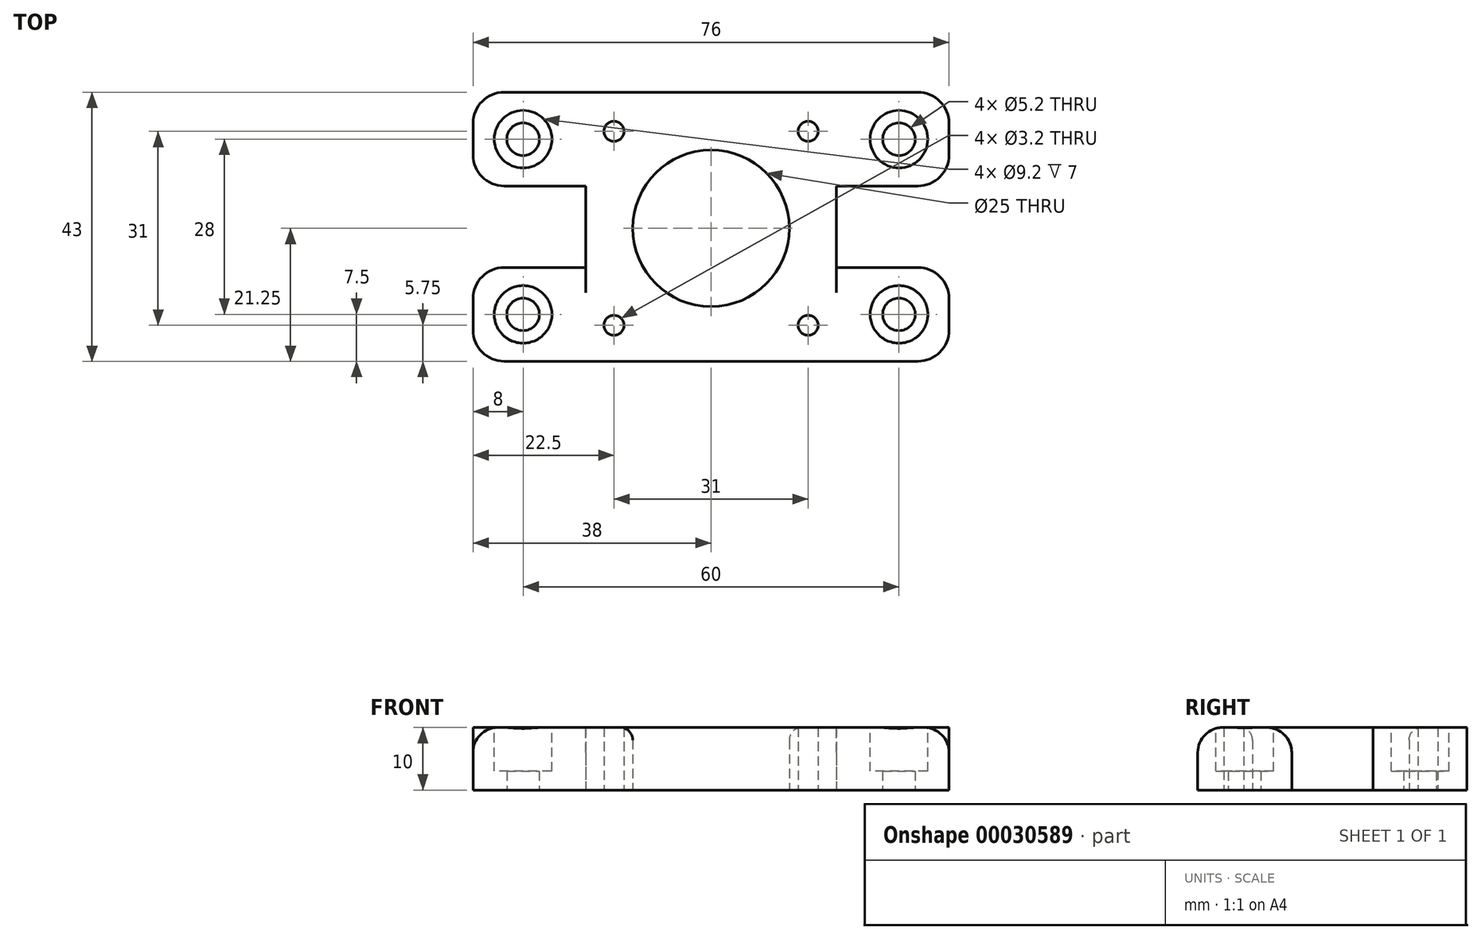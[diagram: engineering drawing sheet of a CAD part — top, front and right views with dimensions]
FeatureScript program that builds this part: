
annotation { "Feature Type Name" : "Feature", "Feature Type Description" : "" }
export const myFeature = defineFeature(function(context is Context, id is Id, definition is map)
    precondition{}
    {
        {
            assignVariable(context, id + "F0", {"name" : "defaultThickness", "anyValue" : 10 * mm});
        }
        {
            var Q0;
            Q0=qCreatedBy(makeId("Top.planeOp"),FACE);
            var sketch = newSketch(context, id + "F1", { "sketchPlane" : qUnion([Q0])});
            skLineSegment(sketch, "E0.rect.bottom", {"start": v(-20, 21.5) * mm, "end": v(20, 21.5) * mm});
            skLineSegment(sketch, "E0.rect.top", {"start": v(-20, -21.5) * mm, "end": v(20, -21.5) * mm});
            skLineSegment(sketch, "E0.rect.left", {"start": v(-20, 21.5) * mm, "end": v(-20, -21.5) * mm});
            skLineSegment(sketch, "E0.rect.right", {"start": v(20, 21.5) * mm, "end": v(20, -21.5) * mm});
            skPoint(sketch, "E0.rect.middle", {"position": v(0, 0) * mm});
            skLineSegment(sketch, "E1", {"start": v(0, 21.5) * mm, "end": v(0, 0) * mm, "construction": true});
            skLineSegment(sketch, "E2", {"start": v(0, -21.5) * mm, "end": v(0, 0) * mm, "construction": true});
            skSolve(sketch);
        }
        {
            var Q0;
            Q0 = qSketchRegion(id + "F1", true);
            extrude(context, id + "F2", {"entities" : qUnion([Q0]), "depth" : getVariable(context, 'defaultThickness')});
        }
        {
            var Q0;
            Q0=makeQuery(id+"F2.opExtrude","CAP_FACE",FACE,{"disambiguationData":[OSD([sQuery(id+"F1.wireOp",EDGE,"E0.rect.bottom"),sQuery(id+"F1.wireOp",EDGE,"E0.rect.top"),sQuery(id+"F1.wireOp",EDGE,"E0.rect.left"),sQuery(id+"F1.wireOp",EDGE,"E0.rect.right"),sQuery(id+"F1.wireOp",EDGE,"f753b575-aba3-41a6-833e-e4f93ea5e4c448.MirrorCS"),sQuery(id+"F1.wireOp",EDGE,"f753b575-aba3-41a6-833e-e4f93ea5e4c449.MirrorC"),sQuery(id+"F1.wireOp",EDGE,"f753b575-aba3-41a6-833e-e4f93ea5e4c450.MirrorCS"),sQuery(id+"F1.wireOp",EDGE,"f753b575-aba3-41a6-833e-e4f93ea5e4c451.MirrorCS"),sQuery(id+"F1.wireOp",EDGE,"bc571038-01dd-487e-b9a0-def5901bd9830.MirrorCS"),sQuery(id+"F1.wireOp",EDGE,"12bf195a-cfe4-4b15-ab7f-3f731c2d51660.MirrorCS"),sQuery(id+"F1.wireOp",EDGE,"455051b4-7426-46a8-a129-8b9c592178470.MirrorCS"),sQuery(id+"F1.wireOp",EDGE,"7dd5bb44-a427-4bdb-ba85-5ced25b216bb0.MirrorC")])],"isStart":true});
            var sketch = newSketch(context, id + "F3", { "sketchPlane" : qUnion([Q0])});
            skLineSegment(sketch, "E3", {"start": v(20, -21.5) * mm, "end": v(20, -21.5) * mm});
            skLineSegment(sketch, "E4", {"start": v(20, -21.5) * mm, "end": v(-20, -21.5) * mm, "construction": true});
            skLineSegment(sketch, "E5", {"start": v(-20, -21.5) * mm, "end": v(-20, -21.5) * mm});
            skLineSegment(sketch, "E6", {"start": v(0, 21.5) * mm, "end": v(0, 0) * mm, "construction": true});
            skLineSegment(sketch, "E7", {"start": v(0, 0) * mm, "end": v(0, -21) * mm, "construction": true});
            skLineSegment(sketch, "E8", {"start": v(0, -21) * mm, "end": v(-20, -21) * mm, "construction": true});
            skLineSegment(sketch, "E9", {"start": v(-20, -21) * mm, "end": v(-20, 21.5) * mm, "construction": true});
            skLineSegment(sketch, "E10", {"start": v(-20, 21.5) * mm, "end": v(0, 21.5) * mm, "construction": true});
            skLineSegment(sketch, "E11", {"start": v(20, 21.5) * mm, "end": v(20, -21) * mm, "construction": true});
            skLineSegment(sketch, "E12", {"start": v(20, -21) * mm, "end": v(0, -21) * mm, "construction": true});
            skLineSegment(sketch, "E13", {"start": v(-20, 0.25) * mm, "end": v(0, 0.25) * mm, "construction": true});
            skLineSegment(sketch, "E14", {"start": v(0, 0.25) * mm, "end": v(20, 0.25) * mm, "construction": true});
            skPoint(sketch, "E15", {"position": v(0, 0.25) * mm});
            skCircle(sketch, "E16", {"center": v(0, 0.25) * mm, "radius": 12.5 * mm});
            skCircle(sketch, "E17", {"center": v(-15.5, -15.25) * mm, "radius": 1.6 * mm});
            skCircle(sketch, "E18", {"center": v(15.5, -15.25) * mm, "radius": 1.6 * mm});
            skCircle(sketch, "E19", {"center": v(15.5, 15.75) * mm, "radius": 1.6 * mm});
            skCircle(sketch, "E20", {"center": v(-15.5, 15.75) * mm, "radius": 1.6 * mm});
            skSolve(sketch);
        }
        {
            var Q0;
            Q0 = qSketchRegion(id + "F3", true);
            extrude(context, id + "F4", {"entities" : qUnion([Q0]), "operationType" : NewBodyOperationType.REMOVE, "endBound" : BoundingType.THROUGH_ALL, "oppositeDirection" : true, "depth" : 25 * mm});
        }
        {
            var Q0;
            Q0=makeQuery(id+"F2.opExtrude","CAP_FACE",FACE,{"disambiguationData":[OSD([sQuery(id+"F1.wireOp",EDGE,"E0.rect.bottom"),sQuery(id+"F1.wireOp",EDGE,"E0.rect.top"),sQuery(id+"F1.wireOp",EDGE,"E0.rect.left"),sQuery(id+"F1.wireOp",EDGE,"E0.rect.right")])],"isStart":true});
            var sketch = newSketch(context, id + "F5", { "sketchPlane" : qUnion([Q0])});
            skLineSegment(sketch, "E21", {"start": v(-20, 21.5) * mm, "end": v(-38, 21.5) * mm});
            skLineSegment(sketch, "E22", {"start": v(-38, 21.5) * mm, "end": v(-38, 6.5) * mm});
            skLineSegment(sketch, "E23", {"start": v(-38, 6.5) * mm, "end": v(-20, 6.5) * mm});
            skLineSegment(sketch, "E24", {"start": v(-20, 21.5) * mm, "end": v(-20, 6.5) * mm});
            skCircle(sketch, "E25", {"center": v(-30, 14) * mm, "radius": 2.6 * mm});
            skLineSegment(sketch, "E26.MirrorCS", {"start": v(20, 21.5) * mm, "end": v(38, 21.5) * mm});
            skLineSegment(sketch, "E27.MirrorCS", {"start": v(38, 6.5) * mm, "end": v(20, 6.5) * mm});
            skCircle(sketch, "E28.MirrorC", {"center": v(30, 14) * mm, "radius": 2.6 * mm});
            skLineSegment(sketch, "E29.MirrorCS", {"start": v(20, 21.5) * mm, "end": v(20, 6.5) * mm});
            skLineSegment(sketch, "E30.MirrorCS", {"start": v(38, 21.5) * mm, "end": v(38, 6.5) * mm});
            skLineSegment(sketch, "E31", {"start": v(-20, -21.5) * mm, "end": v(-38, -21.5) * mm});
            skLineSegment(sketch, "E32", {"start": v(-38, -21.5) * mm, "end": v(-38, -6.5) * mm});
            skLineSegment(sketch, "E33", {"start": v(-38, -6.5) * mm, "end": v(-20, -6.5) * mm});
            skLineSegment(sketch, "E34", {"start": v(-20, -6.5) * mm, "end": v(-20, -21.5) * mm});
            skLineSegment(sketch, "E35.bottom", {"start": v(20, -21.5) * mm, "end": v(38, -21.5) * mm});
            skLineSegment(sketch, "E35.top", {"start": v(20, -6.5) * mm, "end": v(38, -6.5) * mm});
            skLineSegment(sketch, "E35.left", {"start": v(20, -21.5) * mm, "end": v(20, -6.5) * mm});
            skLineSegment(sketch, "E35.right", {"start": v(38, -21.5) * mm, "end": v(38, -6.5) * mm});
            skCircle(sketch, "E36", {"center": v(-30, -14) * mm, "radius": 2.6 * mm});
            skCircle(sketch, "E37", {"center": v(30, -14) * mm, "radius": 2.6 * mm});
            skSolve(sketch);
        }
        {
            var Q0;
            Q0 = qSketchRegion(id + "F5", true);
            extrude(context, id + "F6", {"entities" : qUnion([Q0]), "operationType" : NewBodyOperationType.ADD, "oppositeDirection" : true, "depth" : getVariable(context, 'defaultThickness')});
        }
        {
            var Q0;
            Q0=makeQuery(id+"F2.opExtrude","SWEPT_EDGE",EDGE,{"disambiguationData":[OSD([sQuery(id+"F1.wireOp",EDGE,"f753b575-aba3-41a6-833e-e4f93ea5e4c450.MirrorCS"),sQuery(id+"F1.wireOp",EDGE,"f753b575-aba3-41a6-833e-e4f93ea5e4c451.MirrorCS")])]});
            var Q1;
            Q1=makeQuery(id+"F2.opExtrude","SWEPT_EDGE",EDGE,{"disambiguationData":[OSD([sQuery(id+"F1.wireOp",EDGE,"f753b575-aba3-41a6-833e-e4f93ea5e4c448.MirrorCS"),sQuery(id+"F1.wireOp",EDGE,"f753b575-aba3-41a6-833e-e4f93ea5e4c451.MirrorCS")])]});
            var Q2;
            Q2=makeQuery(id+"F2.opExtrude","SWEPT_EDGE",EDGE,{"disambiguationData":[OSD([sQuery(id+"F1.wireOp",EDGE,"12bf195a-cfe4-4b15-ab7f-3f731c2d51660.MirrorCS"),sQuery(id+"F1.wireOp",EDGE,"455051b4-7426-46a8-a129-8b9c592178470.MirrorCS")])]});
            var Q3;
            Q3=makeQuery(id+"F2.opExtrude","SWEPT_EDGE",EDGE,{"disambiguationData":[OSD([sQuery(id+"F1.wireOp",EDGE,"bc571038-01dd-487e-b9a0-def5901bd9830.MirrorCS"),sQuery(id+"F1.wireOp",EDGE,"12bf195a-cfe4-4b15-ab7f-3f731c2d51660.MirrorCS")])]});
            var Q4;
            Q4=makeQuery(id+"F1IgwxVWLGXEZ05_1.opExtrude","CAP_EDGE",EDGE,{"disambiguationData":[OSD([sQuery(id+"F46VJo8EH1OxCCN_1.wireOp",EDGE,"a8bc6f70-3fce-4169-98be-ded91195f1be.right")])],"isStart":false});
            var Q5;
            Q5=makeQuery(id+"F1IgwxVWLGXEZ05_1.opExtrude","CAP_EDGE",EDGE,{"disambiguationData":[OSD([sQuery(id+"F46VJo8EH1OxCCN_1.wireOp",EDGE,"a8bc6f70-3fce-4169-98be-ded91195f1be.left")])],"isStart":false});
            var Q6;
            Q6=makeQuery(id+"F6.opExtrude","SWEPT_EDGE",EDGE,{"disambiguationData":[OSD([sQuery(id+"F5.wireOp",EDGE,"E26.MirrorCS"),sQuery(id+"F5.wireOp",EDGE,"E30.MirrorCS")])]});
            var Q7;
            Q7=makeQuery(id+"F6.opExtrude","SWEPT_EDGE",EDGE,{"disambiguationData":[OSD([sQuery(id+"F5.wireOp",EDGE,"E27.MirrorCS"),sQuery(id+"F5.wireOp",EDGE,"E30.MirrorCS")])]});
            var Q8;
            Q8=makeQuery(id+"F6.opExtrude","SWEPT_EDGE",EDGE,{"disambiguationData":[OSD([sQuery(id+"F5.wireOp",EDGE,"E22"),sQuery(id+"F5.wireOp",EDGE,"E23")])]});
            var Q9;
            Q9=makeQuery(id+"F6.opExtrude","SWEPT_EDGE",EDGE,{"disambiguationData":[OSD([sQuery(id+"F5.wireOp",EDGE,"E21"),sQuery(id+"F5.wireOp",EDGE,"E22")])]});
            var Q10;
            Q10=makeQuery(id+"F6.opExtrude","SWEPT_EDGE",EDGE,{"disambiguationData":[OSD([sQuery(id+"F5.wireOp",EDGE,"E32"),sQuery(id+"F5.wireOp",EDGE,"E33")])]});
            var Q11;
            Q11=makeQuery(id+"F6.opExtrude","SWEPT_EDGE",EDGE,{"disambiguationData":[OSD([sQuery(id+"F5.wireOp",EDGE,"E31"),sQuery(id+"F5.wireOp",EDGE,"E32")])]});
            var Q12;
            Q12=makeQuery(id+"F6.opExtrude","SWEPT_EDGE",EDGE,{"disambiguationData":[OSD([sQuery(id+"F5.wireOp",EDGE,"E35.top"),sQuery(id+"F5.wireOp",EDGE,"E35.right")])]});
            var Q13;
            Q13=makeQuery(id+"F6.opExtrude","SWEPT_EDGE",EDGE,{"disambiguationData":[OSD([sQuery(id+"F5.wireOp",EDGE,"E35.bottom"),sQuery(id+"F5.wireOp",EDGE,"E35.right")])]});
            var Q14;
            Q14=makeQuery(id+"F6.opExtrude","SWEPT_EDGE",EDGE,{"disambiguationData":[OSD([sQuery(id+"F1.wireOp",EDGE,"E0.rect.right"),sQuery(id+"F5.wireOp",EDGE,"E35.top"),sQuery(id+"F5.wireOp",EDGE,"E35.left")])]});
            var Q15;
            Q15=makeQuery(id+"F6.opExtrude","SWEPT_EDGE",EDGE,{"disambiguationData":[OSD([sQuery(id+"F1.wireOp",EDGE,"E0.rect.right"),sQuery(id+"F5.wireOp",EDGE,"E27.MirrorCS"),sQuery(id+"F5.wireOp",EDGE,"E29.MirrorCS")])]});
            var Q16;
            Q16=makeQuery(id+"F6.opExtrude","SWEPT_EDGE",EDGE,{"disambiguationData":[OSD([sQuery(id+"F1.wireOp",EDGE,"E0.rect.left"),sQuery(id+"F5.wireOp",EDGE,"E33"),sQuery(id+"F5.wireOp",EDGE,"E34")])]});
            var Q17;
            Q17=makeQuery(id+"F6.opExtrude","SWEPT_EDGE",EDGE,{"disambiguationData":[OSD([sQuery(id+"F1.wireOp",EDGE,"E0.rect.left"),sQuery(id+"F5.wireOp",EDGE,"E23"),sQuery(id+"F5.wireOp",EDGE,"E24")])]});
            fillet(context, id + "F7", {"entities" : qUnion([Q0, Q1, Q2, Q3, Q4, Q5, Q6, Q7, Q8, Q9, Q10, Q11, Q12, Q13, Q14, Q15, Q16, Q17]), "radius" : 5 * mm, "tangentPropagation" : true, "allowEdgeOverflow" : false});
        }
        {
            var Q0;
            Q0=makeQuery(id+"F6.boolean.opBoolean","MERGE",FACE,{"derivedFrom":[makeQuery(id+"F2.opExtrude","CAP_FACE",FACE,{"disambiguationData":[OSD([sQuery(id+"F1.wireOp",EDGE,"E0.rect.bottom"),sQuery(id+"F1.wireOp",EDGE,"E0.rect.top"),sQuery(id+"F1.wireOp",EDGE,"E0.rect.left"),sQuery(id+"F1.wireOp",EDGE,"E0.rect.right")])],"isStart":false}),makeQuery(id+"F6.opExtrude","CAP_FACE",FACE,{"disambiguationData":[OSD([sQuery(id+"F5.wireOp",EDGE,"E21"),sQuery(id+"F5.wireOp",EDGE,"E22"),sQuery(id+"F5.wireOp",EDGE,"E23"),sQuery(id+"F5.wireOp",EDGE,"E24"),sQuery(id+"F5.wireOp",EDGE,"E25")])],"isStart":false}),makeQuery(id+"F6.opExtrude","CAP_FACE",FACE,{"disambiguationData":[OSD([sQuery(id+"F5.wireOp",EDGE,"E26.MirrorCS"),sQuery(id+"F5.wireOp",EDGE,"E27.MirrorCS"),sQuery(id+"F5.wireOp",EDGE,"E28.MirrorC"),sQuery(id+"F5.wireOp",EDGE,"E29.MirrorCS"),sQuery(id+"F5.wireOp",EDGE,"E30.MirrorCS")])],"isStart":false}),makeQuery(id+"F6.opExtrude","CAP_FACE",FACE,{"disambiguationData":[OSD([sQuery(id+"F5.wireOp",EDGE,"E31"),sQuery(id+"F5.wireOp",EDGE,"E32"),sQuery(id+"F5.wireOp",EDGE,"E33"),sQuery(id+"F5.wireOp",EDGE,"E34"),sQuery(id+"F5.wireOp",EDGE,"E36")])],"isStart":false}),makeQuery(id+"F6.opExtrude","CAP_FACE",FACE,{"disambiguationData":[OSD([sQuery(id+"F5.wireOp",EDGE,"E35.bottom"),sQuery(id+"F5.wireOp",EDGE,"E35.top"),sQuery(id+"F5.wireOp",EDGE,"E35.left"),sQuery(id+"F5.wireOp",EDGE,"E35.right"),sQuery(id+"F5.wireOp",EDGE,"E37")])],"isStart":false})]});
            var sketch = newSketch(context, id + "F8", { "sketchPlane" : qUnion([Q0])});
            skCircle(sketch, "E38", {"center": v(-30, 14) * mm, "radius": 4.6 * mm});
            skCircle(sketch, "E39", {"center": v(30, 14) * mm, "radius": 4.6 * mm});
            skCircle(sketch, "E40", {"center": v(-30, -14) * mm, "radius": 4.6 * mm});
            skCircle(sketch, "E41", {"center": v(30, -14) * mm, "radius": 4.6 * mm});
            skSolve(sketch);
        }
        {
            var Q0;
            Q0=makeQuery(id+"F8.imprint","IMPRINT",FACE,{"disambiguationData":[TD([[makeQuery(id+"F8.imprint","IMPRINT",EDGE,{"derivedFrom":sQuery(id+"F8.wireOp",EDGE,"E38")}),1.0]])]});
            var Q1;
            Q1=makeQuery(id+"F8.imprint","IMPRINT",FACE,{"disambiguationData":[TD([[makeQuery(id+"F8.imprint","IMPRINT",EDGE,{"derivedFrom":sQuery(id+"F8.wireOp",EDGE,"E40")}),1.0]])]});
            var Q2;
            Q2=makeQuery(id+"F8.imprint","IMPRINT",FACE,{"disambiguationData":[TD([[makeQuery(id+"F8.imprint","IMPRINT",EDGE,{"derivedFrom":sQuery(id+"F8.wireOp",EDGE,"E39")}),1.0]])]});
            var Q3;
            Q3=makeQuery(id+"F8.imprint","IMPRINT",FACE,{"disambiguationData":[TD([[makeQuery(id+"F8.imprint","IMPRINT",EDGE,{"derivedFrom":sQuery(id+"F8.wireOp",EDGE,"E41")}),1.0]])]});
            extrude(context, id + "F9", {"entities" : qUnion([Q0, Q1, Q2, Q3]), "operationType" : NewBodyOperationType.REMOVE, "oppositeDirection" : true, "depth" : 7 * mm});
        }
        {
            var Q0;
            Q0=makeQuery(id+"F9.boolean.opBoolean","COPY",EDGE,{"derivedFrom":makeQuery(id+"F9.opExtrude","CAP_EDGE",EDGE,{"disambiguationData":[OSD([sQuery(id+"F8.wireOp",EDGE,"E39")])],"isStart":true})});
            var Q1;
            Q1=makeQuery(id+"F9.boolean.opBoolean","COPY",EDGE,{"derivedFrom":makeQuery(id+"F9.opExtrude","CAP_EDGE",EDGE,{"disambiguationData":[OSD([sQuery(id+"F8.wireOp",EDGE,"E38")])],"isStart":true})});
            var Q2;
            Q2=makeQuery(id+"F9.boolean.opBoolean","COPY",EDGE,{"derivedFrom":makeQuery(id+"F9.opExtrude","CAP_EDGE",EDGE,{"disambiguationData":[OSD([sQuery(id+"F8.wireOp",EDGE,"E40")])],"isStart":true})});
            var Q3;
            Q3=makeQuery(id+"F9.boolean.opBoolean","COPY",EDGE,{"derivedFrom":makeQuery(id+"F9.opExtrude","CAP_EDGE",EDGE,{"disambiguationData":[OSD([sQuery(id+"F8.wireOp",EDGE,"E41")])],"isStart":true})});
            var Q4;
            Q4=makeQuery(id+"F6.boolean.opBoolean","MERGE",EDGE,{"derivedFrom":[makeQuery(id+"F2.opExtrude","CAP_EDGE",EDGE,{"disambiguationData":[OSD([sQuery(id+"F1.wireOp",EDGE,"E0.rect.top")])],"isStart":false}),makeQuery(id+"F6.opExtrude","CAP_EDGE",EDGE,{"disambiguationData":[OSD([sQuery(id+"F5.wireOp",EDGE,"E21")])],"isStart":false}),makeQuery(id+"F6.opExtrude","CAP_EDGE",EDGE,{"disambiguationData":[OSD([sQuery(id+"F5.wireOp",EDGE,"E26.MirrorCS")])],"isStart":false})]});
            fillet(context, id + "F10", {"entities" : qUnion([Q0, Q1, Q2, Q3, Q4]), "radius" : 4 * mm, "tangentPropagation" : true, "allowEdgeOverflow" : false});
        }
        {
            var Q0;
            Q0=makeQuery(id+"F4.boolean.opBoolean","INTERSECT",EDGE,{"derivedFrom":[makeQuery(id+"F2.opExtrude","CAP_FACE",FACE,{"disambiguationData":[OSD([sQuery(id+"F1.wireOp",EDGE,"E0.rect.bottom"),sQuery(id+"F1.wireOp",EDGE,"E0.rect.top"),sQuery(id+"F1.wireOp",EDGE,"E0.rect.left"),sQuery(id+"F1.wireOp",EDGE,"E0.rect.right")])],"isStart":false}),makeQuery(id+"F4.opExtrude","SWEPT_FACE",FACE,{"disambiguationData":[OSD([sQuery(id+"F3.wireOp",EDGE,"E16")])]})]});
            fillet(context, id + "F11", {"entities" : qUnion([Q0]), "radius" : 2 * mm, "tangentPropagation" : true, "allowEdgeOverflow" : false});
        }
    });
